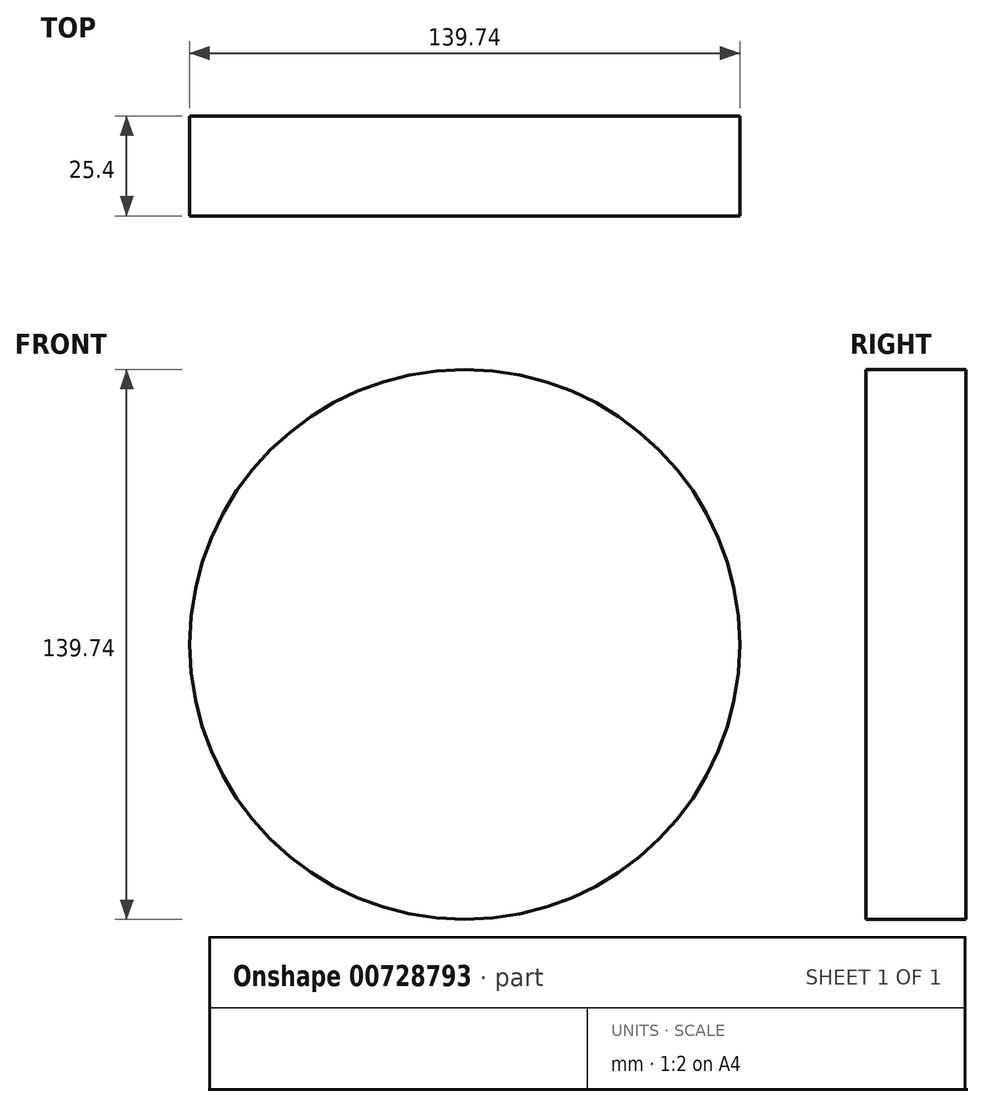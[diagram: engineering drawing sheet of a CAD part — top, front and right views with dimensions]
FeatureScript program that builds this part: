
annotation { "Feature Type Name" : "Feature", "Feature Type Description" : "" }
export const myFeature = defineFeature(function(context is Context, id is Id, definition is map)
    precondition{}
    {
        {
            var Q0;
            Q0=qCreatedBy(makeId("Front.planeOp"),FACE);
            var sketch = newSketch(context, id + "F0", { "sketchPlane" : qUnion([Q0])});
            skCircle(sketch, "E0", {"center": v(0, 0) * mm, "radius": 69.87 * mm});
            skSolve(sketch);
        }
        {
            var Q0;
            Q0 = qSketchRegion(id + "F0", true);
            extrude(context, id + "F1", {"entities" : qUnion([Q0]), "depth" : 25.4 * mm, "offsetDistance" : 25.4 * mm});
        }
    });
